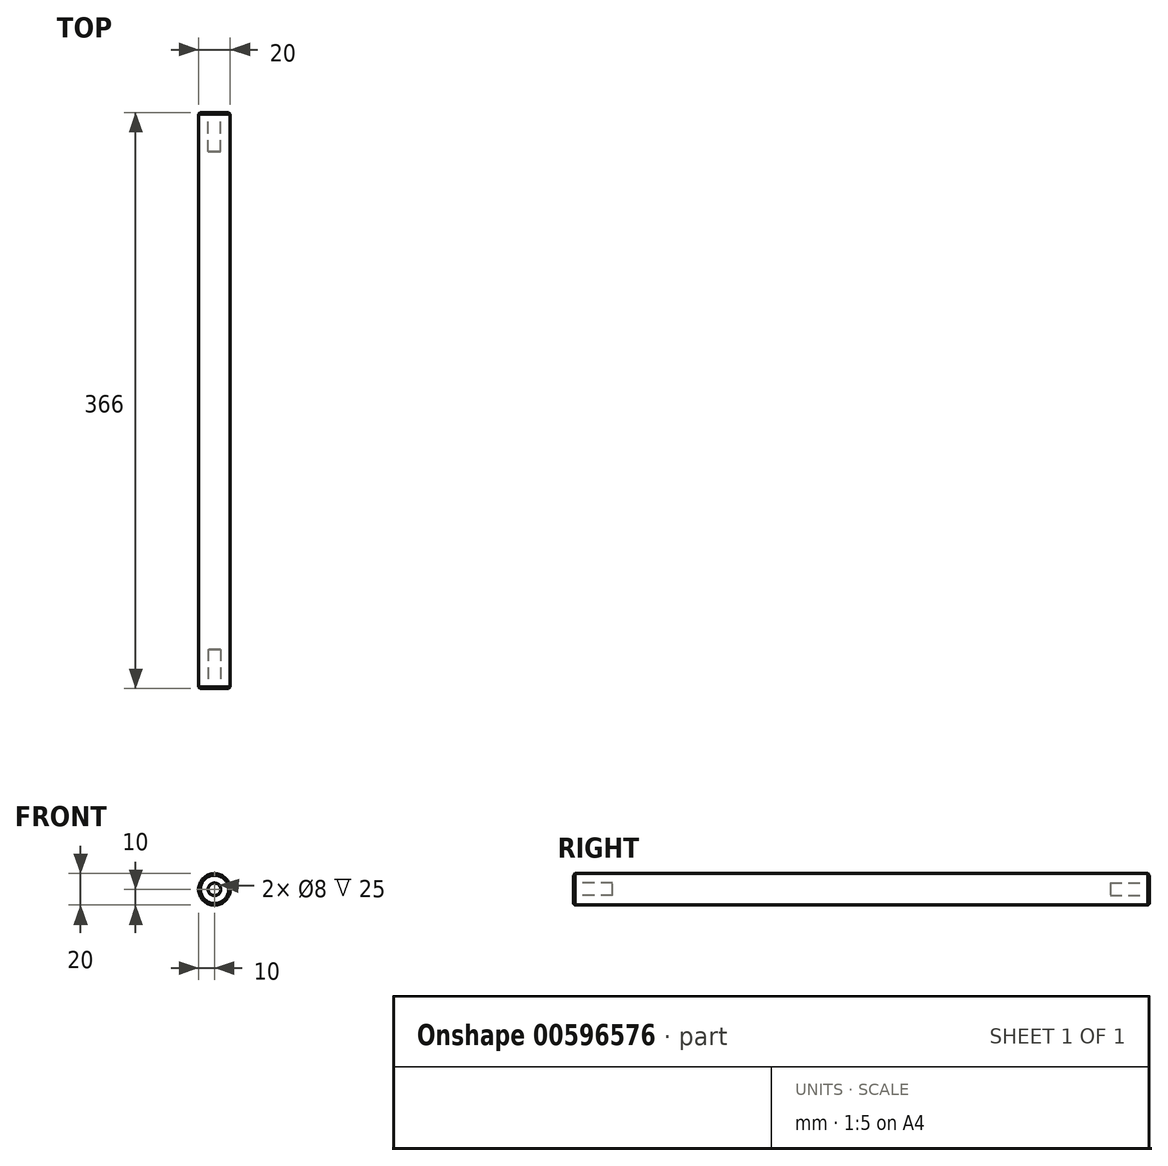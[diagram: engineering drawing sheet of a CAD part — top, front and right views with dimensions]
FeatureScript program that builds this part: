
annotation { "Feature Type Name" : "Feature", "Feature Type Description" : "" }
export const myFeature = defineFeature(function(context is Context, id is Id, definition is map)
    precondition{}
    {
        {
            var Q0;
            Q0=qCreatedBy(makeId("Front.planeOp"),FACE);
            var sketch = newSketch(context, id + "F0", { "sketchPlane" : qUnion([Q0])});
            skCircle(sketch, "E0", {"center": v(0, 0) * mm, "radius": 10 * mm});
            skSolve(sketch);
        }
        {
            var Q0;
            Q0=makeQuery(id+"F0.imprint","IMPRINT",FACE,{"disambiguationData":[TD([[makeQuery(id+"F0.imprint","IMPRINT",EDGE,{"derivedFrom":sQuery(id+"F0.wireOp",EDGE,"E0")}),1.0]])]});
            extrude(context, id + "F1", {"entities" : qUnion([Q0]), "depth" : 366 * mm, "offsetDistance" : 25 * mm});
        }
        {
            var Q0;
            Q0=makeQuery(id+"F1.opExtrude","CAP_EDGE",EDGE,{"disambiguationData":[OSD([sQuery(id+"F0.wireOp",EDGE,"E0")])],"isStart":false});
            var Q1;
            Q1=makeQuery(id+"F1.opExtrude","CAP_EDGE",EDGE,{"disambiguationData":[OSD([sQuery(id+"F0.wireOp",EDGE,"E0")])],"isStart":true});
            chamfer(context, id + "F2", {"entities" : qUnion([Q0, Q1]), "width" : 1 * mm, "tangentPropagation" : true});
        }
        {
            var Q0;
            Q0=makeQuery(id+"F1.opExtrude","CAP_FACE",FACE,{"disambiguationData":[OSD([sQuery(id+"F0.wireOp",EDGE,"E0")])],"isStart":false});
            var sketch = newSketch(context, id + "F3", { "sketchPlane" : qUnion([Q0])});
            skCircle(sketch, "E1", {"center": v(0, 0) * mm, "radius": 4 * mm});
            skSolve(sketch);
        }
        {
            var Q0;
            Q0 = qSketchRegion(id + "F3", true);
            extrude(context, id + "F4", {"entities" : qUnion([Q0]), "operationType" : NewBodyOperationType.REMOVE, "oppositeDirection" : true, "depth" : 25 * mm, "offsetDistance" : 25 * mm});
        }
        {
            var Q0;
            Q0=makeQuery(id+"F1.opExtrude","CAP_FACE",FACE,{"disambiguationData":[OSD([sQuery(id+"F0.wireOp",EDGE,"E0")])],"isStart":true});
            var sketch = newSketch(context, id + "F5", { "sketchPlane" : qUnion([Q0])});
            skCircle(sketch, "E2", {"center": v(0, 0) * mm, "radius": 4 * mm});
            skSolve(sketch);
        }
        {
            var Q0;
            Q0=makeQuery(id+"F5.imprint","IMPRINT",FACE,{"disambiguationData":[TD([[makeQuery(id+"F5.imprint","IMPRINT",EDGE,{"derivedFrom":sQuery(id+"F5.wireOp",EDGE,"E2")}),1.0]])]});
            extrude(context, id + "F6", {"entities" : qUnion([Q0]), "operationType" : NewBodyOperationType.REMOVE, "oppositeDirection" : true, "depth" : 25 * mm, "offsetDistance" : 25 * mm});
        }
    });
